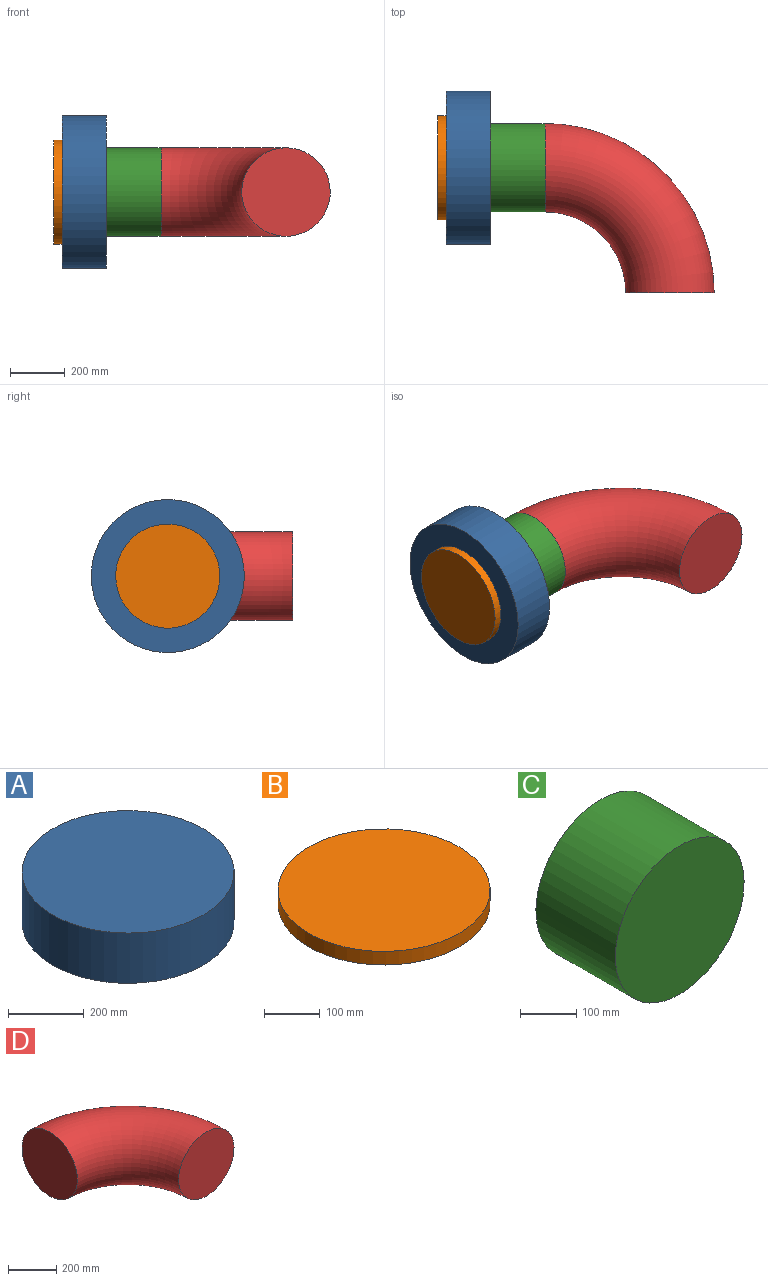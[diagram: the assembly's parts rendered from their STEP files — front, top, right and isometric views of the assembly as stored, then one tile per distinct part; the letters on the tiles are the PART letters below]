
ASSEMBLY  parts=4 mates=3
PART A: 3 faces, bbox 560x560x162.4 mm
  f0: cylinder r=280mm len=560mm, axis (0,0,-1), area 285709mm2, adj f1,f2
  f1: plane 560x560mm, normal (0,0,1), area 246300.9mm2, adj f0
  f2: plane 560x560mm, normal (0,0,-1), area 246300.9mm2, adj f0
PART B: 3 faces, bbox 381x381x30 mm
  f0: cylinder r=190.5mm len=381mm, axis (0,0,-1), area 35908.4mm2, adj f1,f2
  f1: plane 381x381mm, normal (0,0,1), area 114009.2mm2, adj f0
  f2: plane 381x381mm, normal (0,0,-1), area 114009.2mm2, adj f0
PART C: 3 faces, bbox 323.9x200x323.9 mm
  f0: cylinder r=161.95mm len=323.9mm, axis (0,1,0), area 203512.4mm2, adj f1,f2
  f1: plane 323.9x323.9mm, normal (0,-1,0), area 82397.1mm2, adj f0
  f2: plane 323.9x323.9mm, normal (0,1,0), area 82397.1mm2, adj f0
PART D: 3 faces, bbox 670.2x670.2x323.9 mm
  f0: plane 323.9x323.9mm, normal (0,-1,0), area 82397.1mm2, adj f2
  f1: plane 323.9x323.9mm, normal (-1,0,0), area 82397.1mm2, adj f2
  f2: torus R=457.2mm, axis (0,0,1), area 730780.4mm2, adj f0,f1
PLACE A rot(axis=(0,-1,0),90deg) t=(175.44,189.96,12.53)mm
PLACE B rot(axis=(0,-1,0),90deg) t=(13.04,189.96,12.53)mm
PLACE C rot(axis=(0,0,-1),90deg) t=(375.44,189.96,12.53)mm
PLACE D t=(832.64,-267.24,12.53)mm
MATE fastened C.f0 <-> A.f0  axis (1,0,0) through (175.44,189.96,12.53)mm
MATE fastened A.f0 <-> B.f0  axis (-1,0,0) through (13.04,189.96,12.53)mm
MATE fastened D.f1 <-> C.f0  axis (-1,0,0) through (375.44,189.96,12.53)mm
